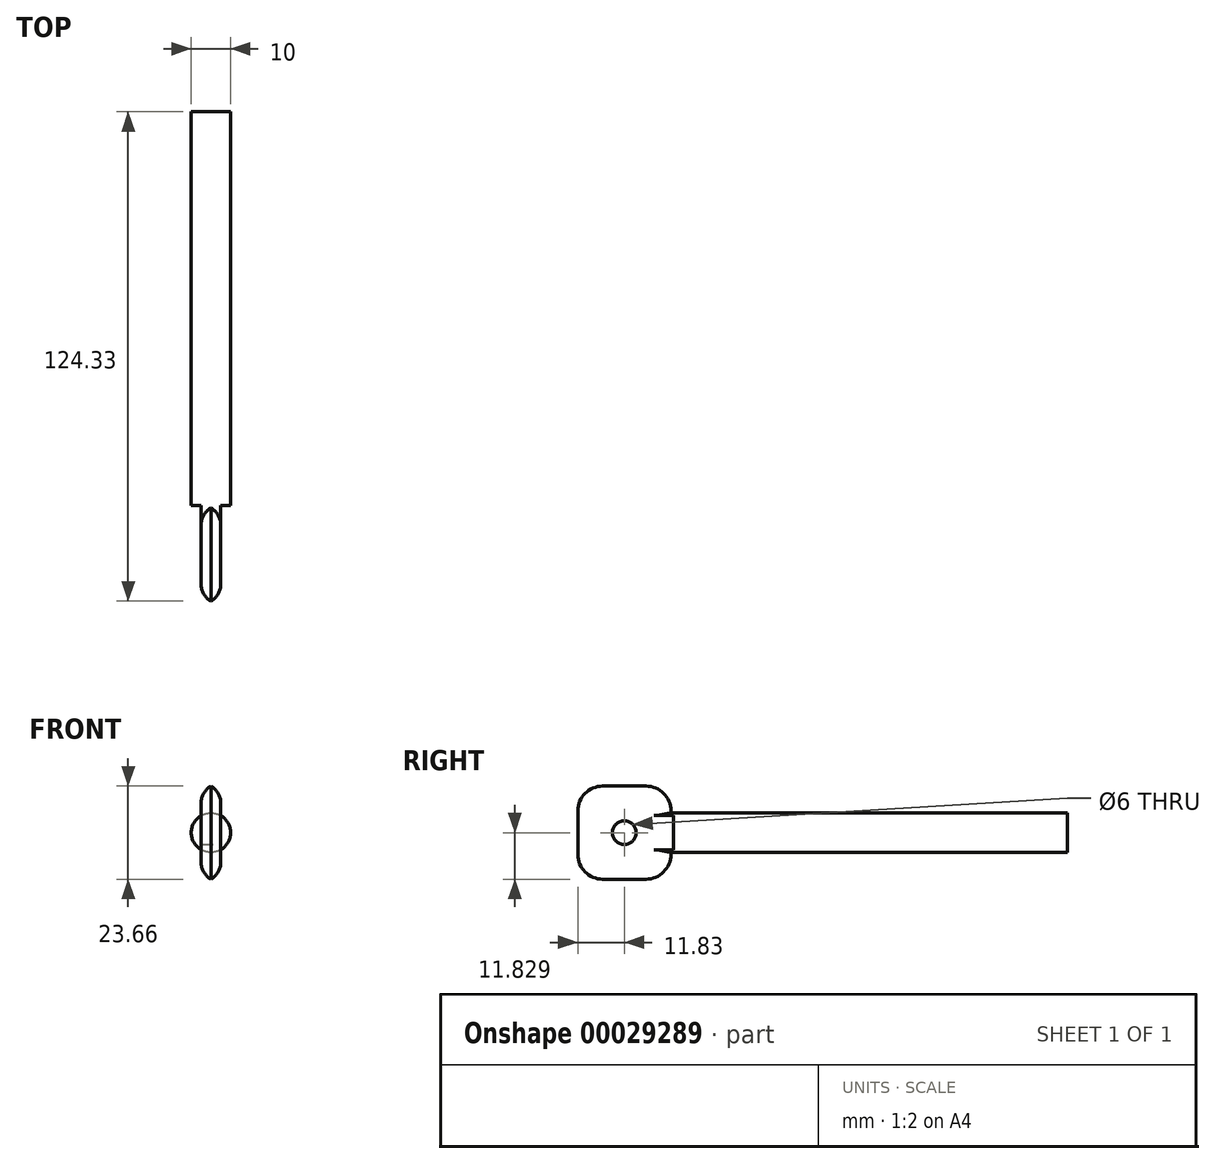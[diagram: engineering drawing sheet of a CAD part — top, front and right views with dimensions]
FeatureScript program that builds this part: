
annotation { "Feature Type Name" : "Feature", "Feature Type Description" : "" }
export const myFeature = defineFeature(function(context is Context, id is Id, definition is map)
    precondition{}
    {
        {
            var Q0;
            Q0=qCreatedBy(makeId("Front.planeOp"),FACE);
            var sketch = newSketch(context, id + "F0", { "sketchPlane" : qUnion([Q0])});
            skCircle(sketch, "E0", {"center": v(19.59, 9.68) * mm, "radius": 5 * mm});
            skSolve(sketch);
        }
        {
            var Q0;
            Q0 = qSketchRegion(id + "F0", true);
            extrude(context, id + "F1", {"entities" : qUnion([Q0]), "depth" : 100 * mm});
        }
        {
            var Q0;
            Q0=makeQuery(id+"F1.opExtrude","CAP_FACE",FACE,{"disambiguationData":[OSD([sQuery(id+"F0.wireOp",EDGE,"E0")])],"isStart":false});
            var sketch = newSketch(context, id + "F2", { "sketchPlane" : qUnion([Q0])});
            skLineSegment(sketch, "E1.bottom", {"start": v(17.09, 22.18) * mm, "end": v(22.09, 22.18) * mm});
            skLineSegment(sketch, "E1.top", {"start": v(17.09, -2.82) * mm, "end": v(22.09, -2.82) * mm});
            skLineSegment(sketch, "E1.left", {"start": v(17.09, 22.18) * mm, "end": v(17.09, -2.82) * mm});
            skLineSegment(sketch, "E1.right", {"start": v(22.09, 22.18) * mm, "end": v(22.09, -2.82) * mm});
            skSolve(sketch);
        }
        {
            var Q0;
            Q0 = qSketchRegion(id + "F2", true);
            extrude(context, id + "F3", {"entities" : qUnion([Q0]), "operationType" : NewBodyOperationType.ADD, "depth" : 25 * mm});
        }
        {
            var Q0;
            Q0=makeQuery(id+"F3.opExtrude","SWEPT_FACE",FACE,{"disambiguationData":[OSD([sQuery(id+"F2.wireOp",EDGE,"E1.right")])]});
            var sketch = newSketch(context, id + "F4", { "sketchPlane" : qUnion([Q0])});
            skCircle(sketch, "E2", {"center": v(-112.5, 9.68) * mm, "radius": 3 * mm});
            skSolve(sketch);
        }
        {
            var Q0;
            Q0 = qSketchRegion(id + "F4", true);
            extrude(context, id + "F5", {"entities" : qUnion([Q0]), "operationType" : NewBodyOperationType.REMOVE, "endBound" : BoundingType.UP_TO_NEXT, "oppositeDirection" : true, "depth" : 25 * mm});
        }
        {
            var Q0;
            Q0=makeQuery(id+"F3.opExtrude","CAP_EDGE",EDGE,{"disambiguationData":[OSD([sQuery(id+"F2.wireOp",EDGE,"E1.bottom")])],"isStart":false});
            var Q1;
            Q1=makeQuery(id+"F3.opExtrude","CAP_EDGE",EDGE,{"disambiguationData":[OSD([sQuery(id+"F2.wireOp",EDGE,"E1.top")])],"isStart":false});
            var Q2;
            Q2=makeQuery(id+"F3.opExtrude","CAP_EDGE",EDGE,{"disambiguationData":[OSD([sQuery(id+"F2.wireOp",EDGE,"E1.bottom")])],"isStart":true});
            var Q3;
            Q3=makeQuery(id+"F3.opExtrude","CAP_EDGE",EDGE,{"disambiguationData":[OSD([sQuery(id+"F2.wireOp",EDGE,"E1.top")])],"isStart":true});
            fillet(context, id + "F6", {"entities" : qUnion([Q0, Q1, Q2, Q3]), "radius" : 7 * mm, "tangentPropagation" : true, "allowEdgeOverflow" : false});
        }
        {
            var Q0;
            {var subQ0=sQuery(id+"F2.wireOp",EDGE,"E1.right");var subQ1=sQuery(id+"F0.wireOp",EDGE,"E0");Q0=makeQuery(id+"F3.boolean.opBoolean","SPLIT",EDGE,{"disambiguationData":[TD([makeQuery(id+"F1.opExtrude","SWEPT_FACE",FACE,{"disambiguationData":[OSD([subQ1])]}),makeQuery(id+"F1.opExtrude","CAP_FACE",FACE,{"disambiguationData":[OSD([subQ1])],"isStart":false}),makeQuery(id+"F3.opExtrude","CAP_FACE",FACE,{"disambiguationData":[OSD([sQuery(id+"F2.wireOp",EDGE,"E1.bottom"),sQuery(id+"F2.wireOp",EDGE,"E1.top"),sQuery(id+"F2.wireOp",EDGE,"E1.left"),subQ0])],"isStart":true}),makeQuery(id+"F3.opExtrude","SWEPT_FACE",FACE,{"disambiguationData":[OSD([subQ0])]})])],"derivedFrom":makeQuery(id+"F3.opExtrude","CAP_EDGE",EDGE,{"disambiguationData":[OSD([subQ0])],"isStart":true})});}
            var Q1;
            {var subQ0=sQuery(id+"F2.wireOp",EDGE,"E1.left");var subQ1=sQuery(id+"F0.wireOp",EDGE,"E0");Q1=makeQuery(id+"F3.boolean.opBoolean","SPLIT",EDGE,{"disambiguationData":[TD([makeQuery(id+"F1.opExtrude","SWEPT_FACE",FACE,{"disambiguationData":[OSD([subQ1])]}),makeQuery(id+"F1.opExtrude","CAP_FACE",FACE,{"disambiguationData":[OSD([subQ1])],"isStart":false}),makeQuery(id+"F3.opExtrude","CAP_FACE",FACE,{"disambiguationData":[OSD([sQuery(id+"F2.wireOp",EDGE,"E1.bottom"),sQuery(id+"F2.wireOp",EDGE,"E1.top"),subQ0,sQuery(id+"F2.wireOp",EDGE,"E1.right")])],"isStart":true}),makeQuery(id+"F3.opExtrude","SWEPT_FACE",FACE,{"disambiguationData":[OSD([subQ0])]})])],"derivedFrom":makeQuery(id+"F3.opExtrude","CAP_EDGE",EDGE,{"disambiguationData":[OSD([subQ0])],"isStart":true})});}
            fillet(context, id + "F7", {"entities" : qUnion([Q0, Q1]), "radius" : 5 * mm, "tangentPropagation" : true, "allowEdgeOverflow" : false});
        }
    });
